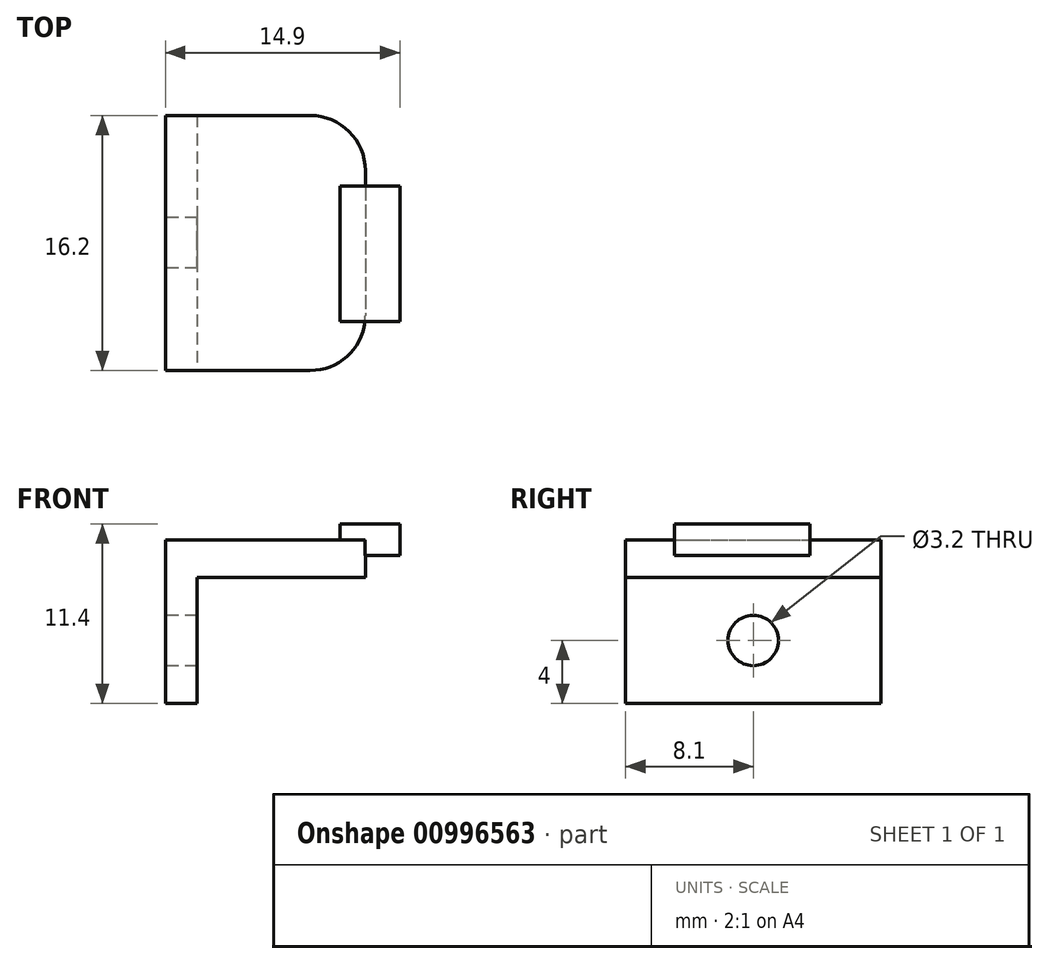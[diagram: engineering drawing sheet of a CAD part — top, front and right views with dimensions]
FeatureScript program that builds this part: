
annotation { "Feature Type Name" : "Feature", "Feature Type Description" : "" }
export const myFeature = defineFeature(function(context is Context, id is Id, definition is map)
    precondition{}
    {
        {
            var Q0;
            Q0=qCreatedBy(makeId("Top.planeOp"),FACE);
            var sketch = newSketch(context, id + "F0", { "sketchPlane" : qUnion([Q0])});
            skLineSegment(sketch, "E0.bottom", {"start": v(18, 8.1) * mm, "end": v(-18, 8.1) * mm});
            skLineSegment(sketch, "E0.top", {"start": v(18, -8.1) * mm, "end": v(-18, -8.1) * mm});
            skLineSegment(sketch, "E0.left", {"start": v(18, 8.1) * mm, "end": v(18, -8.1) * mm});
            skLineSegment(sketch, "E0.right", {"start": v(-18, 8.1) * mm, "end": v(-18, -8.1) * mm});
            skPoint(sketch, "E0.middle", {"position": v(0, 0) * mm});
            skSolve(sketch);
        }
        {
            var Q0;
            Q0 = qSketchRegion(id + "F0", true);
            extrude(context, id + "F1", {"entities" : qUnion([Q0]), "depth" : 2.4 * mm, "offsetDistance" : 25 * mm});
        }
        {
            var Q0;
            Q0=makeQuery(id+"F1.opExtrude","SWEPT_EDGE",EDGE,{"disambiguationData":[OSD([sQuery(id+"F0.wireOp",EDGE,"E0.top"),sQuery(id+"F0.wireOp",EDGE,"E0.right")])]});
            var Q1;
            Q1=makeQuery(id+"F1.opExtrude","SWEPT_EDGE",EDGE,{"disambiguationData":[OSD([sQuery(id+"F0.wireOp",EDGE,"E0.bottom"),sQuery(id+"F0.wireOp",EDGE,"E0.right")])]});
            var Q2;
            Q2=makeQuery(id+"F1.opExtrude","SWEPT_EDGE",EDGE,{"disambiguationData":[OSD([sQuery(id+"F0.wireOp",EDGE,"E0.top"),sQuery(id+"F0.wireOp",EDGE,"E0.left")])]});
            var Q3;
            Q3=makeQuery(id+"F1.opExtrude","SWEPT_EDGE",EDGE,{"disambiguationData":[OSD([sQuery(id+"F0.wireOp",EDGE,"E0.bottom"),sQuery(id+"F0.wireOp",EDGE,"E0.left")])]});
            fillet(context, id + "F2", {"entities" : qUnion([Q0, Q1, Q2, Q3]), "radius" : 3.5 * mm, "tangentPropagation" : true, "allowEdgeOverflow" : false});
        }
        {
            var Q0;
            Q0=makeQuery(id+"F1.opExtrude","SWEPT_FACE",FACE,{"disambiguationData":[OSD([sQuery(id+"F0.wireOp",EDGE,"E0.bottom")])]});
            cPlane(context, id + "F3", {"entities" : qUnion([Q0]), "cplaneType" : CPlaneType.OFFSET, "offset" : 4.5 * mm, "oppositeDirection" : true, "width" : 150 * mm, "height" : 150 * mm});
        }
        {
            var Q0;
            Q0=qCreatedBy(id+"F3.planeOp",FACE);
            var sketch = newSketch(context, id + "F4", { "sketchPlane" : qUnion([Q0])});
            skLineSegment(sketch, "E1", {"start": v(0, 0) * mm, "end": v(0, 12.36) * mm, "construction": true});
            skLineSegment(sketch, "E2", {"start": v(-20.2, 3.4) * mm, "end": v(-16.4, 3.4) * mm});
            skLineSegment(sketch, "E3", {"start": v(-16.4, 3.4) * mm, "end": v(-16.4, 1.4) * mm});
            skLineSegment(sketch, "E4", {"start": v(-16.4, 1.4) * mm, "end": v(-20.2, 1.4) * mm});
            skLineSegment(sketch, "E5", {"start": v(-20.2, 1.4) * mm, "end": v(-20.2, 3.4) * mm});
            skLineSegment(sketch, "E6.MirrorCS", {"start": v(16.4, 1.4) * mm, "end": v(20.2, 1.4) * mm});
            skLineSegment(sketch, "E7.MirrorCS", {"start": v(20.2, 3.4) * mm, "end": v(16.4, 3.4) * mm});
            skLineSegment(sketch, "E8.MirrorCS", {"start": v(20.2, 1.4) * mm, "end": v(20.2, 3.4) * mm});
            skLineSegment(sketch, "E9.MirrorCS", {"start": v(16.4, 3.4) * mm, "end": v(16.4, 1.4) * mm});
            skSolve(sketch);
        }
        {
            var Q0;
            Q0 = qSketchRegion(id + "F4", true);
            extrude(context, id + "F5", {"entities" : qUnion([Q0]), "operationType" : NewBodyOperationType.ADD, "oppositeDirection" : true, "depth" : 8.6 * mm, "offsetDistance" : 25 * mm});
        }
        {
            var Q0;
            Q0=qCreatedBy(makeId("Top.planeOp"),FACE);
            var sketch = newSketch(context, id + "F6", { "sketchPlane" : qUnion([Q0])});
            skLineSegment(sketch, "E10.bottom", {"start": v(5.3, 8.1) * mm, "end": v(20.2, 8.1) * mm});
            skLineSegment(sketch, "E10.top", {"start": v(5.3, -8.1) * mm, "end": v(20.2, -8.1) * mm});
            skLineSegment(sketch, "E10.left", {"start": v(5.3, 8.1) * mm, "end": v(5.3, -8.1) * mm});
            skLineSegment(sketch, "E10.right", {"start": v(20.2, 8.1) * mm, "end": v(20.2, -8.1) * mm});
            skPoint(sketch, "E10.middle", {"position": v(12.75, 0) * mm});
            skSolve(sketch);
        }
        {
            var Q0;
            Q0=makeQuery(id+"F1.opExtrude","CAP_FACE",FACE,{"disambiguationData":[OSD([sQuery(id+"F0.wireOp",EDGE,"E0.bottom"),sQuery(id+"F0.wireOp",EDGE,"E0.top"),sQuery(id+"F0.wireOp",EDGE,"E0.left"),sQuery(id+"F0.wireOp",EDGE,"E0.right")])],"isStart":true});
            var sketch = newSketch(context, id + "F7", { "sketchPlane" : qUnion([Q0])});
            skLineSegment(sketch, "E11.bottom", {"start": v(7.3, -8.1) * mm, "end": v(-7.3, -8.1) * mm});
            skLineSegment(sketch, "E11.top", {"start": v(7.3, 8.1) * mm, "end": v(-7.3, 8.1) * mm});
            skLineSegment(sketch, "E11.left", {"start": v(-7.3, -8.1) * mm, "end": v(-7.3, 8.1) * mm});
            skLineSegment(sketch, "E11.right", {"start": v(7.3, -8.1) * mm, "end": v(7.3, 8.1) * mm});
            skPoint(sketch, "E11.middle", {"position": v(0, 0) * mm});
            skSolve(sketch);
        }
        {
            var Q0;
            Q0 = qSketchRegion(id + "F7", true);
            extrude(context, id + "F8", {"entities" : qUnion([Q0]), "operationType" : NewBodyOperationType.ADD, "depth" : 8 * mm, "offsetDistance" : 25 * mm});
        }
        {
            var Q0;
            Q0=makeQuery(id+"F8.opExtrude","SWEPT_FACE",FACE,{"disambiguationData":[OSD([sQuery(id+"F7.wireOp",EDGE,"E11.left")])]});
            var sketch = newSketch(context, id + "F9", { "sketchPlane" : qUnion([Q0])});
            skLineSegment(sketch, "E12", {"start": v(-8.1, -8) * mm, "end": v(8.1, 0) * mm, "construction": true});
            skCircle(sketch, "E13", {"center": v(0, -4) * mm, "radius": 1.6 * mm});
            skSolve(sketch);
        }
        {
            var Q0;
            Q0 = qSketchRegion(id + "F9", true);
            extrude(context, id + "F10", {"entities" : qUnion([Q0]), "operationType" : NewBodyOperationType.REMOVE, "endBound" : BoundingType.UP_TO_NEXT, "oppositeDirection" : true, "depth" : 25 * mm, "offsetDistance" : 25 * mm});
        }
        {
            var Q0;
            Q0 = qSketchRegion(id + "F6", true);
            extrude(context, id + "F11", {"entities" : qUnion([Q0]), "operationType" : NewBodyOperationType.INTERSECT, "endBound" : BoundingType.THROUGH_ALL, "depth" : 25 * mm, "offsetDistance" : 25 * mm, "hasSecondDirection" : true, "secondDirectionBound" : SecondDirectionBoundingType.THROUGH_ALL, "secondDirectionOppositeDirection" : true, "secondDirectionDepth" : 25 * mm});
        }
    });
